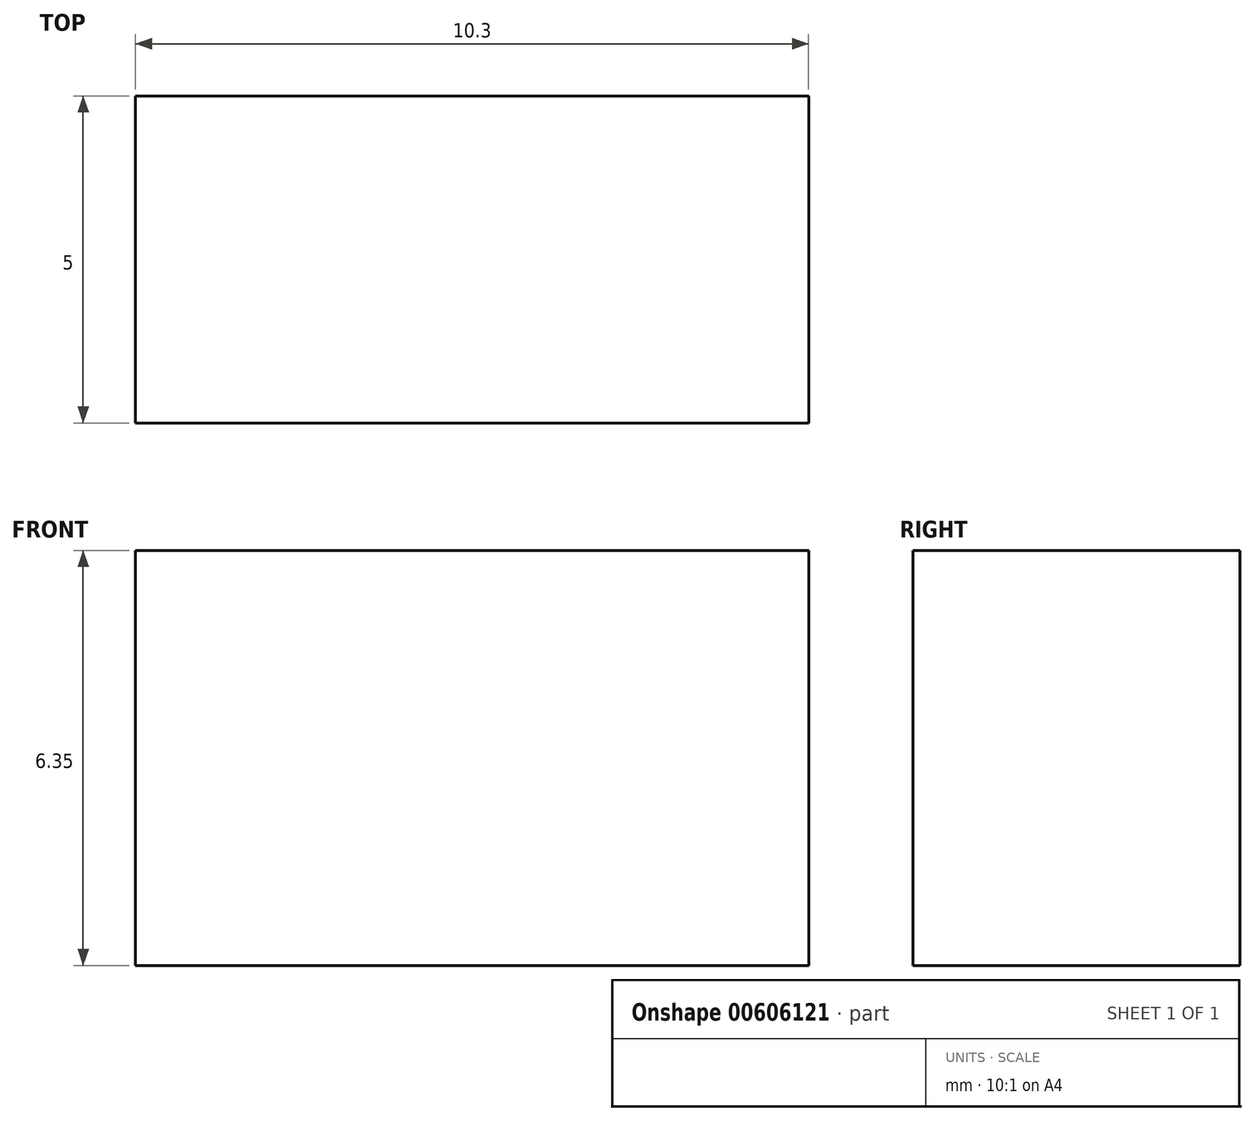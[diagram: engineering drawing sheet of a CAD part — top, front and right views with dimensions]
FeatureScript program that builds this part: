
annotation { "Feature Type Name" : "Feature", "Feature Type Description" : "" }
export const myFeature = defineFeature(function(context is Context, id is Id, definition is map)
    precondition{}
    {
        {
            var Q0;
            Q0=qCreatedBy(makeId("Top.planeOp"),FACE);
            var sketch = newSketch(context, id + "F0", { "sketchPlane" : qUnion([Q0])});
            skLineSegment(sketch, "E0", {"start": v(-5.15, -2.5) * mm, "end": v(5.15, -2.5) * mm});
            skLineSegment(sketch, "E1", {"start": v(5.15, -2.5) * mm, "end": v(5.15, 2.5) * mm});
            skLineSegment(sketch, "E2", {"start": v(5.15, 2.5) * mm, "end": v(-5.15, 2.5) * mm});
            skLineSegment(sketch, "E3", {"start": v(-5.15, 2.5) * mm, "end": v(-5.15, -2.5) * mm});
            skSolve(sketch);
        }
        {
            var Q0;
            Q0=makeQuery(id+"F0.imprint","IMPRINT",FACE,{"disambiguationData":[TD([[makeQuery(id+"F0.imprint","IMPRINT",EDGE,{"derivedFrom":sQuery(id+"F0.wireOp",EDGE,"E0")}),1.0]])]});
            extrude(context, id + "F1", {"entities" : qUnion([Q0]), "depth" : 6.35 * mm, "offsetDistance" : 25.4 * mm});
        }
    });
